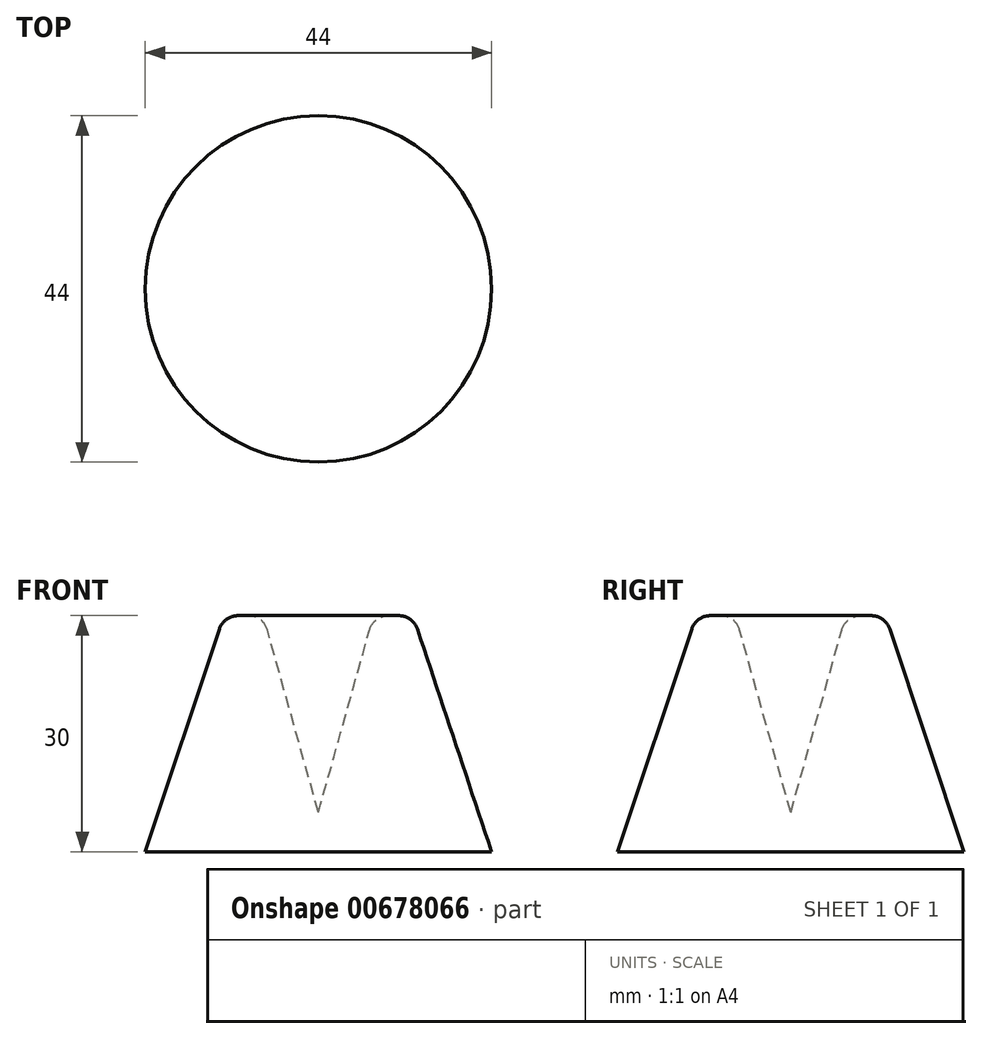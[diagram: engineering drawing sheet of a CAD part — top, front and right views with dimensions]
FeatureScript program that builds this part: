
annotation { "Feature Type Name" : "Feature", "Feature Type Description" : "" }
export const myFeature = defineFeature(function(context is Context, id is Id, definition is map)
    precondition{}
    {
        {
            var Q0;
            Q0=qCreatedBy(makeId("Front.planeOp"),FACE);
            var sketch = newSketch(context, id + "F0", { "sketchPlane" : qUnion([Q0])});
            skLineSegment(sketch, "E0", {"start": v(0, 0) * mm, "end": v(22, 0) * mm});
            skLineSegment(sketch, "E1", {"start": v(0, 0) * mm, "end": v(0, 61.1) * mm, "construction": true});
            skLineSegment(sketch, "E2", {"start": v(22, 0) * mm, "end": v(12, 30) * mm});
            skLineSegment(sketch, "E3", {"start": v(12, 30) * mm, "end": v(7, 30) * mm});
            skLineSegment(sketch, "E4", {"start": v(7, 30) * mm, "end": v(0, 5) * mm});
            skLineSegment(sketch, "E5", {"start": v(0, 5) * mm, "end": v(0, 0) * mm});
            skSolve(sketch);
        }
        {
            var Q0;
            Q0=makeQuery(id+"F0.imprint","IMPRINT",FACE,{"disambiguationData":[TD([[makeQuery(id+"F0.imprint","IMPRINT",EDGE,{"derivedFrom":sQuery(id+"F0.wireOp",EDGE,"E0")}),1.0]])]});
            var Q1;
            Q1=sQuery(id+"F0.wireOp",EDGE,"E5");
            revolve(context, id + "F1", {"entities" : qUnion([Q0]), "axis" : qUnion([Q1]), "revolveType" : RevolveType.FULL});
        }
        {
            var Q0;
            Q0=makeQuery(id+"F1.opRevolve","SWEPT_EDGE",EDGE,{"disambiguationData":[OSD([sQuery(id+"F0.wireOp",EDGE,"E2"),sQuery(id+"F0.wireOp",EDGE,"E3")])]});
            var Q1;
            Q1=makeQuery(id+"F1.opRevolve","SWEPT_EDGE",EDGE,{"disambiguationData":[OSD([sQuery(id+"F0.wireOp",EDGE,"E3"),sQuery(id+"F0.wireOp",EDGE,"E4")])]});
            fillet(context, id + "F2", {"entities" : qUnion([Q0, Q1]), "radius" : 2.5 * mm, "tangentPropagation" : true, "allowEdgeOverflow" : false});
        }
    });
